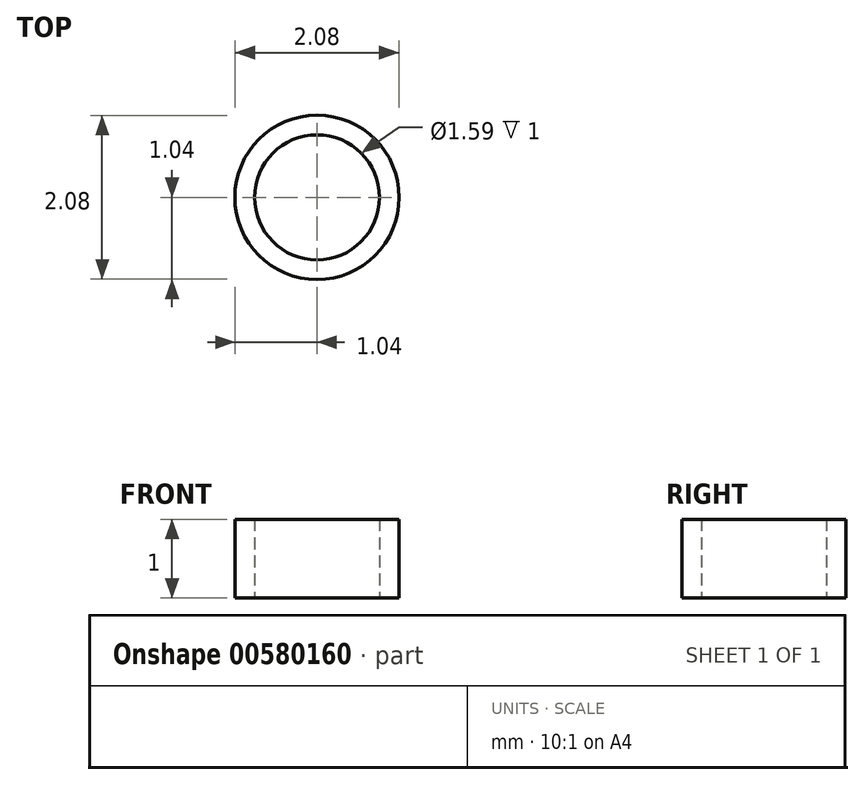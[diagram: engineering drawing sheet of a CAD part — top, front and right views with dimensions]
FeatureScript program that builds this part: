
annotation { "Feature Type Name" : "Feature", "Feature Type Description" : "" }
export const myFeature = defineFeature(function(context is Context, id is Id, definition is map)
    precondition{}
    {
        {
            var Q0;
            Q0=qCreatedBy(makeId("Top.planeOp"),FACE);
            var sketch = newSketch(context, id + "F0", { "sketchPlane" : qUnion([Q0])});
            skCircle(sketch, "E0", {"center": v(0, 0) * mm, "radius": 0.8 * mm});
            skCircle(sketch, "E1.0", {"center": v(0, 0) * mm, "radius": 1.04 * mm});
            skSolve(sketch);
        }
        {
            var Q0;
            Q0=makeQuery(id+"F0.imprint","IMPRINT",FACE,{"disambiguationData":[TD([[makeQuery(id+"F0.imprint","IMPRINT",EDGE,{"derivedFrom":sQuery(id+"F0.wireOp",EDGE,"E0")}),-1.0]])]});
            extrude(context, id + "F1", {"entities" : qUnion([Q0]), "depth" : 1 * mm, "offsetDistance" : 25 * mm});
        }
    });
